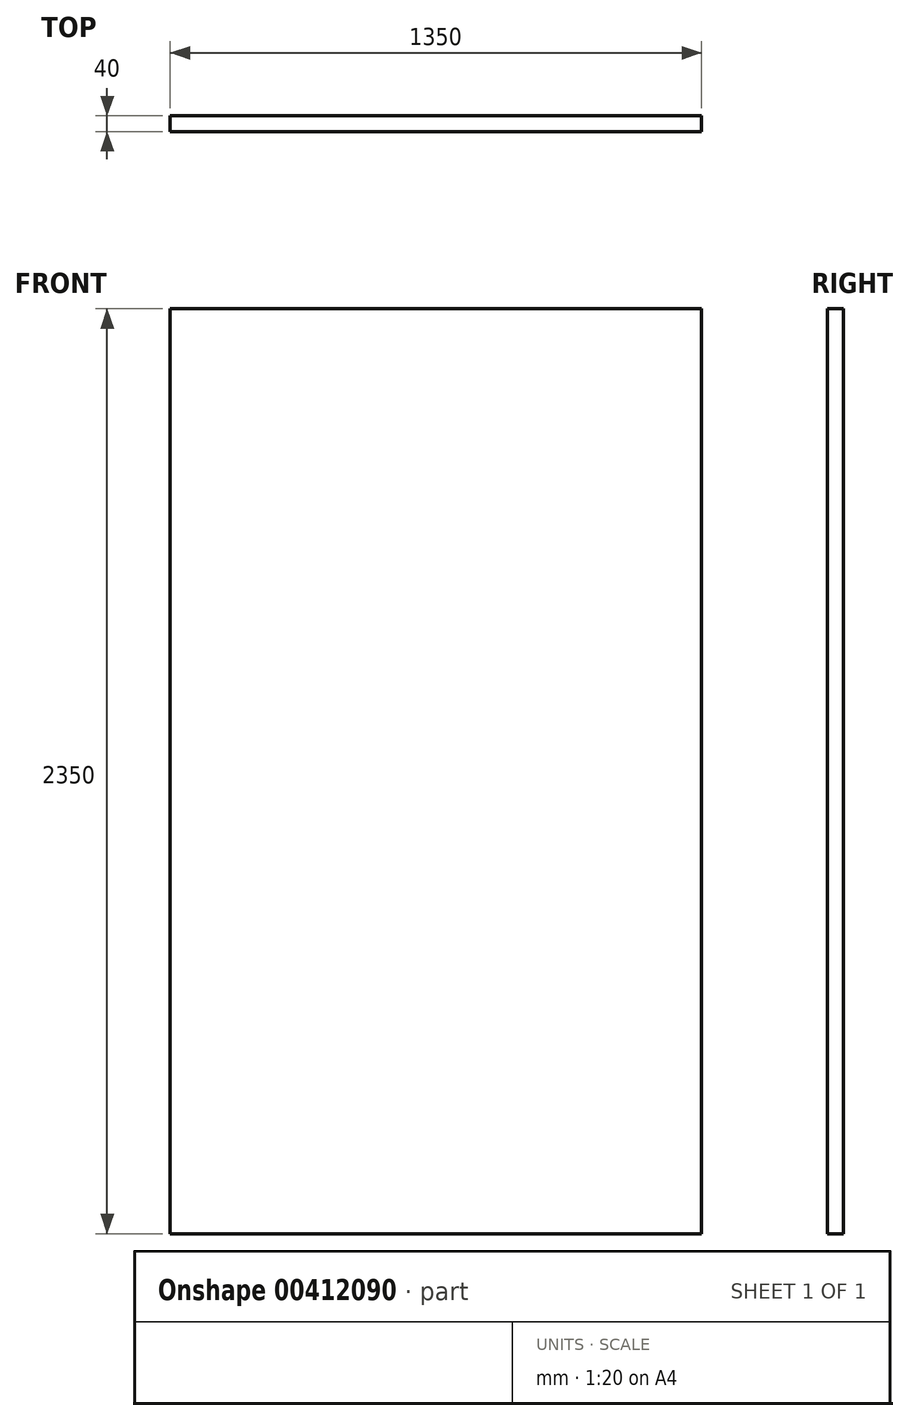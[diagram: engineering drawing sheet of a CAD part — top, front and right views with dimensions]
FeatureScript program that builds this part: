
annotation { "Feature Type Name" : "Feature", "Feature Type Description" : "" }
export const myFeature = defineFeature(function(context is Context, id is Id, definition is map)
    precondition{}
    {
        {
            var Q0;
            Q0=qCreatedBy(makeId("Top.planeOp"),FACE);
            var sketch = newSketch(context, id + "F0", { "sketchPlane" : qUnion([Q0])});
            skLineSegment(sketch, "E0.bottom", {"start": v(-1351.5, -21.5) * mm, "end": v(-1.5, -21.5) * mm});
            skLineSegment(sketch, "E0.top", {"start": v(-1351.5, -61.5) * mm, "end": v(-1.5, -61.5) * mm});
            skLineSegment(sketch, "E0.left", {"start": v(-1351.5, -21.5) * mm, "end": v(-1351.5, -61.5) * mm});
            skLineSegment(sketch, "E0.right", {"start": v(-1.5, -21.5) * mm, "end": v(-1.5, -61.5) * mm});
            skSolve(sketch);
        }
        {
            var Q0;
            Q0 = qSketchRegion(id + "F0", true);
            extrude(context, id + "F1", {"entities" : qUnion([Q0]), "depth" : 2350 * mm});
        }
    });
